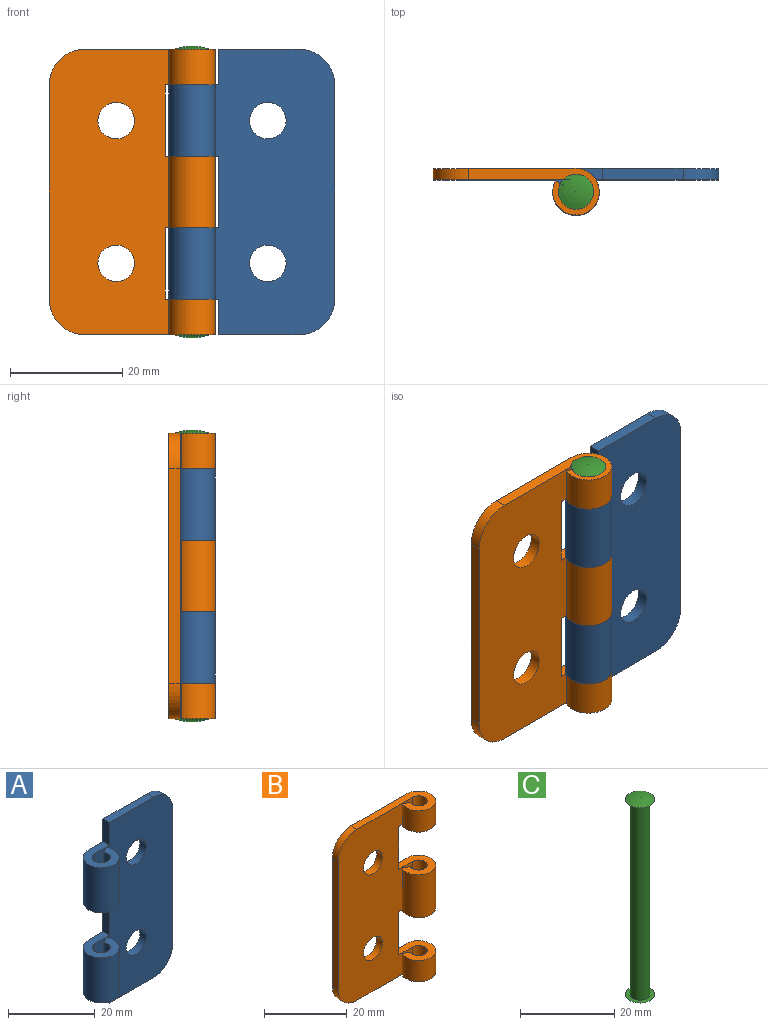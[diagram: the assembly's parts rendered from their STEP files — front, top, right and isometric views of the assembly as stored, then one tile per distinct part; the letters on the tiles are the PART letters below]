
ASSEMBLY  parts=3 mates=2
PART A: 22 faces, bbox 29.5x8.3x50.8 mm
  f0: plane 50.8x25.4mm, normal (0,1,0), area 1086.6mm2, adj f2,f3,f6,f9,f10,f11,f12,f13
  f1: plane 50.8x25.4mm, normal (0,-1,0), area 1086.6mm2, adj f3,f4,f7,f9,f10,f11,f12,f13
  f2: cylinder r=4.14mm len=12.7mm, axis (0,0,-1), area 273.3mm2, adj f0,f5,f13,f18
  f3: plane 38.1x2.03mm, normal (1,0,0), area 77.4mm2, adj f0,f1,f11,f14
  f4: cylinder r=2.11mm len=12.7mm, axis (0,0,-1), area 139.1mm2, adj f1,f5,f13,f18
  f5: plane 12.7x1.79mm, normal (-0.47,0.88,0), area 25.8mm2, adj f2,f4,f13,f18
  f6: cylinder r=4.14mm len=12.7mm, axis (0,0,-1), area 273.3mm2, adj f0,f8,f16,f19
  f7: cylinder r=2.11mm len=12.7mm, axis (0,0,-1), area 139.1mm2, adj f1,f8,f16,f19
  f8: plane 12.7x1.79mm, normal (-0.47,0.88,0), area 25.8mm2, adj f6,f7,f16,f19
  f9: plane 14.33x2.03mm, normal (0,0,1), area 29.1mm2, adj f0,f1,f14,f15
  f10: plane 14.33x2.03mm, normal (0,0,-1), area 29.1mm2, adj f0,f1,f11,f12
  f11: cylinder r=6.35mm len=6.35mm, axis (0,1,0), area 20.3mm2, adj f0,f1,f3,f10
  f12: plane 6.35x2.03mm, normal (-1,0,0), area 12.9mm2, adj f0,f1,f10,f13
  f13: plane 8.86x8.28mm, normal (0,0,-1), area 42.6mm2, adj f0,f1,f2,f4,f5,f12
  f14: cylinder r=6.35mm len=6.35mm, axis (0,1,0), area 20.3mm2, adj f0,f1,f3,f9
  f15: plane 6.35x2.03mm, normal (-1,0,0), area 12.9mm2, adj f0,f1,f9,f16
  f16: plane 8.86x8.28mm, normal (0,0,1), area 42.6mm2, adj f0,f1,f6,f7,f8,f15
  f17: plane 12.7x2.03mm, normal (-1,0,0), area 25.8mm2, adj f0,f1,f18,f19
  f18: plane 8.86x8.28mm, normal (0,0,1), area 42.6mm2, adj f0,f1,f2,f4,f5,f17
  f19: plane 8.86x8.28mm, normal (0,0,-1), area 42.6mm2, adj f0,f1,f6,f7,f8,f17
  f20: cylinder r=3.25mm len=6.5mm, axis (0,1,0), area 41.5mm2, adj f0,f1
  f21: cylinder r=3.25mm len=6.5mm, axis (0,1,0), area 41.5mm2, adj f0,f1
PART B: 24 faces, bbox 29.5x8.3x50.8 mm
  f0: plane 50.8x25.4mm, normal (0,-1,0), area 1086.6mm2, adj f2,f3,f8,f9,f12,f13,f14,f15
  f1: plane 50.8x25.4mm, normal (0,1,0), area 1086.6mm2, adj f6,f7,f8,f11,f12,f13,f14,f15
  f2: cylinder r=2.11mm len=12.7mm, axis (0,0,-1), area 139.1mm2, adj f0,f4,f17,f19
  f3: cylinder r=2.11mm len=6.35mm, axis (0,0,-1), area 69.5mm2, adj f0,f5,f13,f21
  f4: plane 12.7x1.79mm, normal (0.47,0.88,0), area 25.8mm2, adj f2,f6,f17,f19
  f5: plane 6.35x1.79mm, normal (0.47,0.88,0), area 12.9mm2, adj f3,f7,f13,f21
  f6: cylinder r=4.14mm len=12.7mm, axis (0,0,-1), area 273.3mm2, adj f1,f4,f17,f19
  f7: cylinder r=4.14mm len=8.28mm, axis (0,0,-1), area 136.6mm2, adj f1,f5,f13,f21
  f8: plane 38.1x2.03mm, normal (-1,0,0), area 77.4mm2, adj f0,f1,f14,f15
  f9: cylinder r=2.11mm len=6.35mm, axis (0,0,-1), area 69.5mm2, adj f0,f10,f12,f16
  f10: plane 6.35x1.79mm, normal (0.47,0.88,0), area 12.9mm2, adj f9,f11,f12,f16
  f11: cylinder r=4.14mm len=8.28mm, axis (0,0,-1), area 136.6mm2, adj f1,f10,f12,f16
  f12: plane 23.19x8.28mm, normal (0,0,1), area 71.7mm2, adj f0,f1,f9,f10,f11,f15
  f13: plane 23.19x8.28mm, normal (0,0,-1), area 71.7mm2, adj f0,f1,f3,f5,f7,f14
  f14: cylinder r=6.35mm len=6.35mm, axis (0,1,0), area 20.3mm2, adj f0,f1,f8,f13
  f15: cylinder r=6.35mm len=6.35mm, axis (0,1,0), area 20.3mm2, adj f0,f1,f8,f12
  f16: plane 8.86x8.28mm, normal (0,0,-1), area 42.6mm2, adj f0,f1,f9,f10,f11,f18
  f17: plane 8.86x8.28mm, normal (0,0,1), area 42.6mm2, adj f0,f1,f2,f4,f6,f18
  f18: plane 12.7x2.03mm, normal (1,0,0), area 25.8mm2, adj f0,f1,f16,f17
  f19: plane 8.86x8.28mm, normal (0,0,-1), area 42.6mm2, adj f0,f1,f2,f4,f6,f20
  f20: plane 12.7x2.03mm, normal (1,0,0), area 25.8mm2, adj f0,f1,f19,f21
  f21: plane 8.86x8.28mm, normal (0,0,1), area 42.6mm2, adj f0,f1,f3,f5,f7,f20
  f22: cylinder r=3.25mm len=6.5mm, axis (0,1,0), area 41.5mm2, adj f0,f1
  f23: cylinder r=3.25mm len=6.5mm, axis (0,1,0), area 41.5mm2, adj f0,f1
PART C: 5 faces, bbox 6.2x6.2x51.9 mm
  f0: torus R=0mm, axis (0,0,1), area 31.6mm2, adj f1
  f1: plane 6.25x6.25mm, normal (0,0,1), area 16.7mm2, adj f0,f2
  f2: cylinder r=2.11mm len=50.8mm, axis (0,0,1), area 672.9mm2, adj f1,f3
  f3: plane 6.25x6.25mm, normal (0,0,-1), area 16.7mm2, adj f2,f4
  f4: torus R=0mm, axis (0,0,1), area 31.6mm2, adj f3
PLACE A t=(-2.82,6.11,5.2)mm
PLACE B t=(-2.82,6.11,5.2)mm fixed
PLACE C t=(-2.82,1.97,5.2)mm
MATE revolute A.f2 <-> C.f0  axis (0,0,1) through (-2.82,1.97,24.25)mm
MATE fastened B.f6 <-> C.f0  axis (0,0,1) through (-2.82,1.97,30.6)mm
